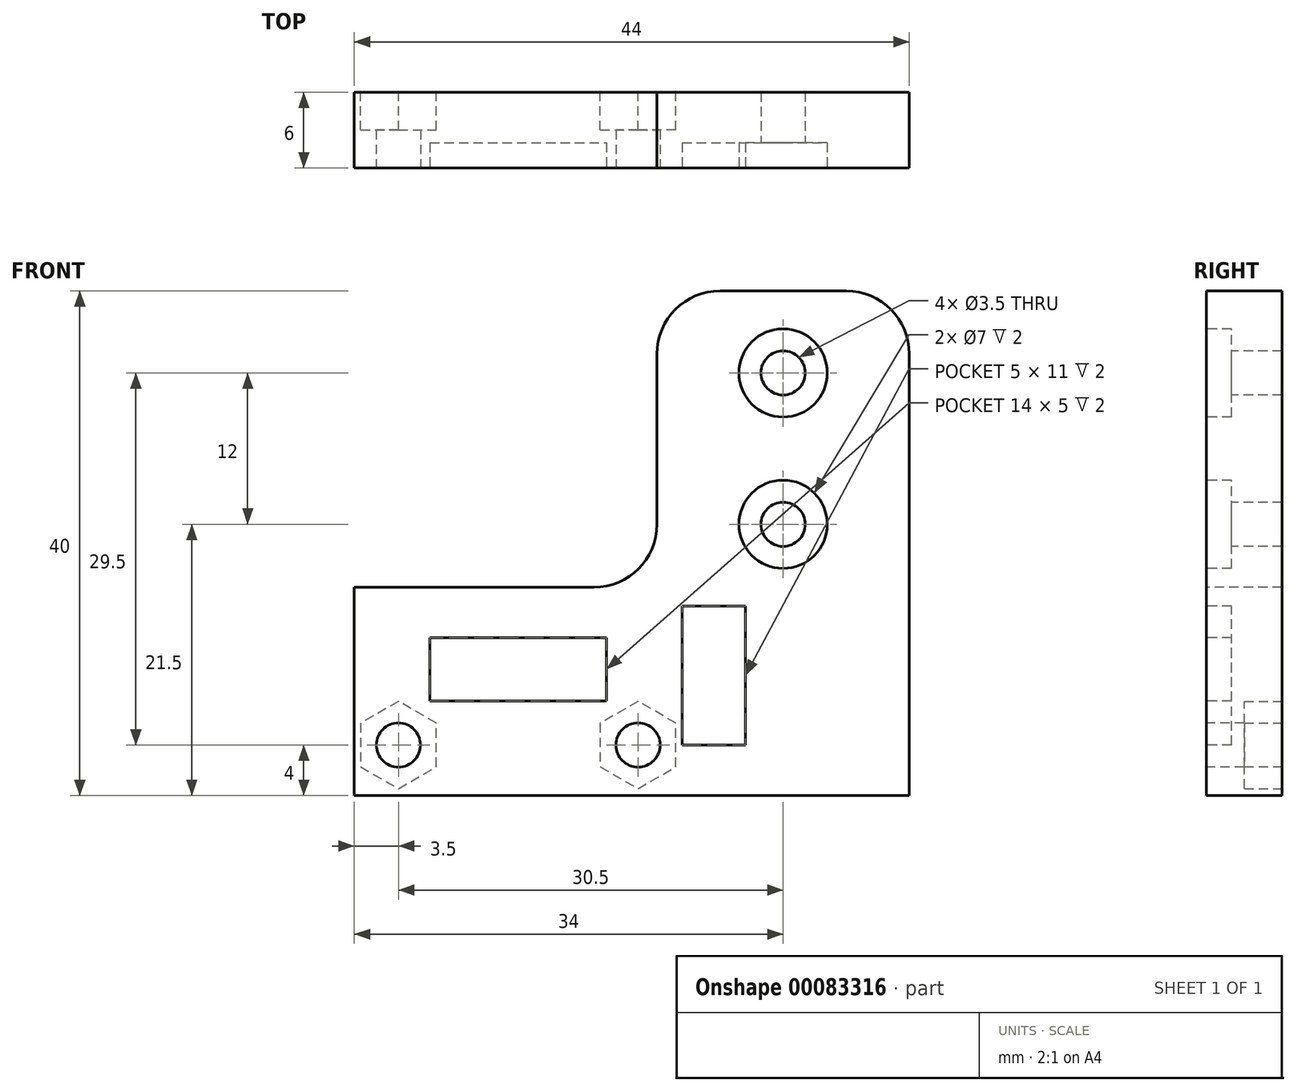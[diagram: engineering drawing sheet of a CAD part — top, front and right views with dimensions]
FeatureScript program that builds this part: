
annotation { "Feature Type Name" : "Feature", "Feature Type Description" : "" }
export const myFeature = defineFeature(function(context is Context, id is Id, definition is map)
    precondition{}
    {
        {
            var Q0;
            Q0=qCreatedBy(makeId("Front.planeOp"),FACE);
            var sketch = newSketch(context, id + "F0", { "sketchPlane" : qUnion([Q0])});
            skLineSegment(sketch, "E0.top", {"start": v(22, -20) * mm, "end": v(-22, -20) * mm});
            skLineSegment(sketch, "E0.left", {"start": v(22, 20) * mm, "end": v(22, -20) * mm});
            skPoint(sketch, "E0.middle", {"position": v(0, 0) * mm});
            skLineSegment(sketch, "E1", {"start": v(-22, -18.5) * mm, "end": v(22, -18.5) * mm, "construction": true});
            skLineSegment(sketch, "E2", {"start": v(-22, -16) * mm, "end": v(22, -16) * mm, "construction": true});
            skCircle(sketch, "E3", {"center": v(-18.5, -16) * mm, "radius": 1.75 * mm});
            skCircle(sketch, "E4", {"center": v(0.5, -16) * mm, "radius": 1.75 * mm});
            skLineSegment(sketch, "E5.bottom", {"start": v(4, -16) * mm, "end": v(9, -16) * mm});
            skLineSegment(sketch, "E5.top", {"start": v(4, -5) * mm, "end": v(9, -5) * mm});
            skLineSegment(sketch, "E5.left", {"start": v(4, -16) * mm, "end": v(4, -5) * mm});
            skLineSegment(sketch, "E5.right", {"start": v(9, -16) * mm, "end": v(9, -5) * mm});
            skLineSegment(sketch, "E6.bottom", {"start": v(-16, -12.5) * mm, "end": v(-2, -12.5) * mm});
            skLineSegment(sketch, "E6.top", {"start": v(-16, -7.5) * mm, "end": v(-2, -7.5) * mm});
            skLineSegment(sketch, "E6.left", {"start": v(-16, -12.5) * mm, "end": v(-16, -7.5) * mm});
            skLineSegment(sketch, "E6.right", {"start": v(-2, -12.5) * mm, "end": v(-2, -7.5) * mm});
            skCircle(sketch, "E7", {"center": v(12, 13.5) * mm, "radius": 1.75 * mm});
            skCircle(sketch, "E8", {"center": v(12, 1.5) * mm, "radius": 1.75 * mm});
            skCircle(sketch, "E9", {"center": v(12, 13.5) * mm, "radius": 3.5 * mm});
            skCircle(sketch, "E10", {"center": v(12, 1.5) * mm, "radius": 3.5 * mm});
            skLineSegment(sketch, "E11", {"start": v(-22, -20) * mm, "end": v(-22, -3.5) * mm});
            skLineSegment(sketch, "E12", {"start": v(-22, -3.5) * mm, "end": v(2, -3.5) * mm});
            skLineSegment(sketch, "E13", {"start": v(2, -3.5) * mm, "end": v(2, 20) * mm});
            skLineSegment(sketch, "E14", {"start": v(2, 20) * mm, "end": v(22, 20) * mm});
            skSolve(sketch);
        }
        {
            var Q0;
            Q0=makeQuery(id+"F0.imprint","IMPRINT",FACE,{"disambiguationData":[TD([[makeQuery(id+"F0.imprint","IMPRINT",EDGE,{"derivedFrom":sQuery(id+"F0.wireOp",EDGE,"E0.top")}),-1.0]])]});
            var Q1;
            Q1=makeQuery(id+"F0.imprint","IMPRINT",FACE,{"disambiguationData":[TD([[makeQuery(id+"F0.imprint","IMPRINT",EDGE,{"derivedFrom":sQuery(id+"F0.wireOp",EDGE,"E6.bottom")}),1.0]])]});
            var Q2;
            Q2=makeQuery(id+"F0.imprint","IMPRINT",FACE,{"disambiguationData":[TD([[makeQuery(id+"F0.imprint","IMPRINT",EDGE,{"derivedFrom":sQuery(id+"F0.wireOp",EDGE,"E5.bottom")}),1.0]])]});
            var Q3;
            Q3=makeQuery(id+"F0.imprint","IMPRINT",FACE,{"disambiguationData":[TD([[makeQuery(id+"F0.imprint","IMPRINT",EDGE,{"derivedFrom":sQuery(id+"F0.wireOp",EDGE,"E8")}),-1.0]])]});
            var Q4;
            Q4=makeQuery(id+"F0.imprint","IMPRINT",FACE,{"disambiguationData":[TD([[makeQuery(id+"F0.imprint","IMPRINT",EDGE,{"derivedFrom":sQuery(id+"F0.wireOp",EDGE,"E7")}),-1.0]])]});
            extrude(context, id + "F1", {"entities" : qUnion([Q0, Q1, Q2, Q3, Q4]), "oppositeDirection" : true, "depth" : 6 * mm});
        }
        {
            var Q0;
            Q0=makeQuery(id+"F0.imprint","IMPRINT",FACE,{"disambiguationData":[TD([[makeQuery(id+"F0.imprint","IMPRINT",EDGE,{"derivedFrom":sQuery(id+"F0.wireOp",EDGE,"E5.bottom")}),1.0]])]});
            var Q1;
            Q1=makeQuery(id+"F0.imprint","IMPRINT",FACE,{"disambiguationData":[TD([[makeQuery(id+"F0.imprint","IMPRINT",EDGE,{"derivedFrom":sQuery(id+"F0.wireOp",EDGE,"E6.bottom")}),1.0]])]});
            var Q2;
            Q2=makeQuery(id+"F0.imprint","IMPRINT",FACE,{"disambiguationData":[TD([[makeQuery(id+"F0.imprint","IMPRINT",EDGE,{"derivedFrom":sQuery(id+"F0.wireOp",EDGE,"E7")}),-1.0]])]});
            var Q3;
            Q3=makeQuery(id+"F0.imprint","IMPRINT",FACE,{"disambiguationData":[TD([[makeQuery(id+"F0.imprint","IMPRINT",EDGE,{"derivedFrom":sQuery(id+"F0.wireOp",EDGE,"E8")}),-1.0]])]});
            extrude(context, id + "F2", {"entities" : qUnion([Q0, Q1, Q2, Q3]), "operationType" : NewBodyOperationType.REMOVE, "oppositeDirection" : true, "depth" : 2 * mm});
        }
        {
            var Q0;
            Q0=makeQuery(id+"F1.opExtrude","CAP_FACE",FACE,{"disambiguationData":[OSD([sQuery(id+"F0.wireOp",EDGE,"E0.top"),sQuery(id+"F0.wireOp",EDGE,"E0.left"),sQuery(id+"F0.wireOp",EDGE,"E3"),sQuery(id+"F0.wireOp",EDGE,"E4"),sQuery(id+"F0.wireOp",EDGE,"E7"),sQuery(id+"F0.wireOp",EDGE,"E8"),sQuery(id+"F0.wireOp",EDGE,"E11"),sQuery(id+"F0.wireOp",EDGE,"E12"),sQuery(id+"F0.wireOp",EDGE,"E13"),sQuery(id+"F0.wireOp",EDGE,"E14")])],"isStart":false});
            var sketch = newSketch(context, id + "F3", { "sketchPlane" : qUnion([Q0])});
            skCircle(sketch, "E15.cCircle", {"center": v(-0.5, -16) * mm, "radius": 3 * mm, "construction": true});
            skLineSegment(sketch, "E15.0", {"start": v(-3.5, -14.27) * mm, "end": v(-0.5, -12.54) * mm});
            skLineSegment(sketch, "E15.1", {"start": v(-0.5, -12.54) * mm, "end": v(2.5, -14.27) * mm});
            skLineSegment(sketch, "E15.2", {"start": v(2.5, -14.27) * mm, "end": v(2.5, -17.73) * mm});
            skLineSegment(sketch, "E15.3", {"start": v(2.5, -17.73) * mm, "end": v(-0.5, -19.46) * mm});
            skLineSegment(sketch, "E15.4", {"start": v(-0.5, -19.46) * mm, "end": v(-3.5, -17.73) * mm});
            skLineSegment(sketch, "E15.5", {"start": v(-3.5, -17.73) * mm, "end": v(-3.5, -14.27) * mm});
            skPoint(sketch, "E15.0.midPoint", {"position": v(-2, -13.4) * mm});
            skCircle(sketch, "E16.cCircle", {"center": v(18.5, -16) * mm, "radius": 3 * mm, "construction": true});
            skLineSegment(sketch, "E16.0", {"start": v(15.5, -17.73) * mm, "end": v(15.5, -14.27) * mm});
            skLineSegment(sketch, "E16.1", {"start": v(15.5, -14.27) * mm, "end": v(18.5, -12.54) * mm});
            skLineSegment(sketch, "E16.2", {"start": v(18.5, -12.54) * mm, "end": v(21.5, -14.27) * mm});
            skLineSegment(sketch, "E16.3", {"start": v(21.5, -14.27) * mm, "end": v(21.5, -17.73) * mm});
            skLineSegment(sketch, "E16.4", {"start": v(21.5, -17.73) * mm, "end": v(18.5, -19.46) * mm});
            skLineSegment(sketch, "E16.5", {"start": v(18.5, -19.46) * mm, "end": v(15.5, -17.73) * mm});
            skPoint(sketch, "E16.0.midPoint", {"position": v(15.5, -16) * mm});
            skSolve(sketch);
        }
        {
            var Q0;
            Q0 = qSketchRegion(id + "F3", true);
            extrude(context, id + "F4", {"entities" : qUnion([Q0]), "operationType" : NewBodyOperationType.REMOVE, "oppositeDirection" : true, "depth" : 3 * mm});
        }
        {
            var Q0;
            Q0=makeQuery(id+"F1.opExtrude","SWEPT_EDGE",EDGE,{"disambiguationData":[OSD([sQuery(id+"F0.wireOp",EDGE,"E12"),sQuery(id+"F0.wireOp",EDGE,"E13")])]});
            var Q1;
            Q1=makeQuery(id+"F1.opExtrude","SWEPT_EDGE",EDGE,{"disambiguationData":[OSD([sQuery(id+"F0.wireOp",EDGE,"E13"),sQuery(id+"F0.wireOp",EDGE,"E14")])]});
            var Q2;
            Q2=makeQuery(id+"F1.opExtrude","SWEPT_EDGE",EDGE,{"disambiguationData":[OSD([sQuery(id+"F0.wireOp",EDGE,"E0.left"),sQuery(id+"F0.wireOp",EDGE,"E14")])]});
            fillet(context, id + "F5", {"entities" : qUnion([Q0, Q1, Q2]), "radius" : 5 * mm, "tangentPropagation" : true, "allowEdgeOverflow" : false});
        }
    });
